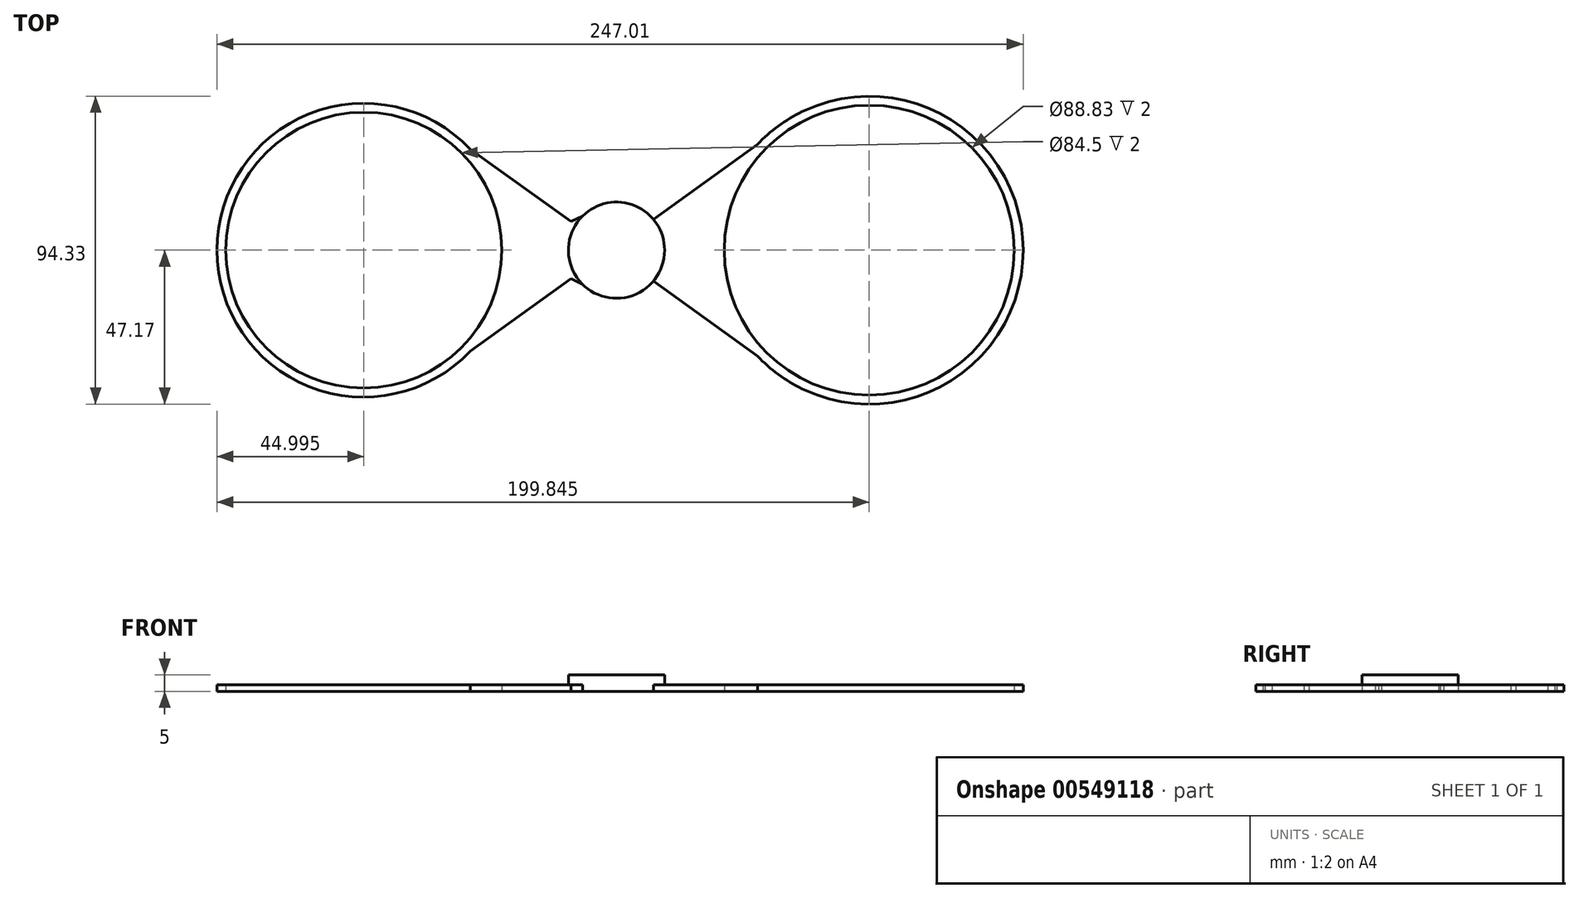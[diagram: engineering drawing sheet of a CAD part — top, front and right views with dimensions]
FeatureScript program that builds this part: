
annotation { "Feature Type Name" : "Feature", "Feature Type Description" : "" }
export const myFeature = defineFeature(function(context is Context, id is Id, definition is map)
    precondition{}
    {
        {
            var Q0;
            Q0=qCreatedBy(makeId("Top.planeOp"),FACE);
            var sketch = newSketch(context, id + "F0", { "sketchPlane" : qUnion([Q0])});
            skCircle(sketch, "E0", {"center": v(77.42, 0) * mm, "radius": 47.16 * mm});
            skCircle(sketch, "E1", {"center": v(-77.43, 0) * mm, "radius": 45 * mm});
            skCircle(sketch, "E2", {"center": v(-77.43, 0) * mm, "radius": 42.25 * mm});
            skCircle(sketch, "E3", {"center": v(77.42, 0) * mm, "radius": 44.41 * mm});
            skPoint(sketch, "E4", {"position": v(-32.43, 0) * mm});
            skPoint(sketch, "E5", {"position": v(30.26, 0) * mm});
            skLineSegment(sketch, "E6", {"start": v(-77.43, 0) * mm, "end": v(-58.4, 40.78) * mm});
            skLineSegment(sketch, "E7", {"start": v(-77.43, 0) * mm, "end": v(-58.4, -40.78) * mm});
            skLineSegment(sketch, "E8", {"start": v(77.42, 0) * mm, "end": v(57.5, -42.75) * mm});
            skLineSegment(sketch, "E9", {"start": v(77.42, 0) * mm, "end": v(57.5, 42.75) * mm});
            skLineSegment(sketch, "E10", {"start": v(-58.4, 40.78) * mm, "end": v(57.5, -42.75) * mm});
            skLineSegment(sketch, "E11", {"start": v(57.5, 42.75) * mm, "end": v(-58.4, -40.78) * mm});
            skLineSegment(sketch, "E12", {"start": v(-32.43, 0) * mm, "end": v(57.5, 42.75) * mm});
            skLineSegment(sketch, "E13", {"start": v(30.26, 0) * mm, "end": v(-58.4, -40.78) * mm});
            skLineSegment(sketch, "E14", {"start": v(-32.43, 0) * mm, "end": v(57.5, -42.75) * mm});
            skLineSegment(sketch, "E15", {"start": v(30.26, 0) * mm, "end": v(-58.4, 40.78) * mm});
            skSolve(sketch);
        }
        {
            var Q0;
            {var subQ1=sQuery(id+"F0.wireOp",EDGE,"E0");var subQ3=sQuery(id+"F0.wireOp",EDGE,"E10");var subQ4=makeQuery(id+"F0.imprint","INTERSECT",VERTEX,{"derivedFrom":[subQ1,subQ3]});Q0=makeQuery(id+"F0.imprint","IMPRINT",FACE,{"disambiguationData":[TD([[makeQuery(id+"F0.imprint","IMPRINT",EDGE,{"disambiguationData":[TD([[subQ4,1.0]])],"derivedFrom":subQ3}),1.0]])]});}
            var Q1;
            {var subQ1=sQuery(id+"F0.wireOp",EDGE,"E13");var subQ3=sQuery(id+"F0.wireOp",EDGE,"HmEMSvIh-oE6Y-JeN1-VhMK-6YFaZQDYRGXj");var subQ4=makeQuery(id+"F0.imprint","INTERSECT",VERTEX,{"disambiguationData":[OD(1.0)],"derivedFrom":[subQ1,subQ3]});Q1=makeQuery(id+"F0.imprint","IMPRINT",FACE,{"disambiguationData":[TD([[makeQuery(id+"F0.imprint","IMPRINT",EDGE,{"disambiguationData":[TD([[subQ4,-1.0]])],"derivedFrom":subQ3}),-1.0]])]});}
            var Q2;
            {var subQ1=sQuery(id+"F0.wireOp",EDGE,"E0");var subQ3=sQuery(id+"F0.wireOp",EDGE,"E11");var subQ4=makeQuery(id+"F0.imprint","INTERSECT",VERTEX,{"derivedFrom":[subQ1,subQ3]});Q2=makeQuery(id+"F0.imprint","IMPRINT",FACE,{"disambiguationData":[TD([[makeQuery(id+"F0.imprint","IMPRINT",EDGE,{"disambiguationData":[TD([[subQ4,-1.0]])],"derivedFrom":subQ3}),1.0]])]});}
            var Q3;
            {var subQ1=sQuery(id+"F0.wireOp",EDGE,"E1");var subQ3=sQuery(id+"F0.wireOp",EDGE,"E10");var subQ4=makeQuery(id+"F0.imprint","INTERSECT",VERTEX,{"derivedFrom":[subQ1,subQ3]});Q3=makeQuery(id+"F0.imprint","IMPRINT",FACE,{"disambiguationData":[TD([[makeQuery(id+"F0.imprint","IMPRINT",EDGE,{"disambiguationData":[TD([[subQ4,-1.0]])],"derivedFrom":subQ3}),-1.0]])]});}
            var Q4;
            {var subQ1=sQuery(id+"F0.wireOp",EDGE,"E12");var subQ3=sQuery(id+"F0.wireOp",EDGE,"HmEMSvIh-oE6Y-JeN1-VhMK-6YFaZQDYRGXj");var subQ4=makeQuery(id+"F0.imprint","INTERSECT",VERTEX,{"disambiguationData":[OD(1.0)],"derivedFrom":[subQ1,subQ3]});Q4=makeQuery(id+"F0.imprint","IMPRINT",FACE,{"disambiguationData":[TD([[makeQuery(id+"F0.imprint","IMPRINT",EDGE,{"disambiguationData":[TD([[subQ4,-1.0]])],"derivedFrom":subQ3}),-1.0]])]});}
            var Q5;
            {var subQ1=sQuery(id+"F0.wireOp",EDGE,"E1");var subQ3=sQuery(id+"F0.wireOp",EDGE,"E11");var subQ4=makeQuery(id+"F0.imprint","INTERSECT",VERTEX,{"derivedFrom":[subQ1,subQ3]});Q5=makeQuery(id+"F0.imprint","IMPRINT",FACE,{"disambiguationData":[TD([[makeQuery(id+"F0.imprint","IMPRINT",EDGE,{"disambiguationData":[TD([[subQ4,1.0]])],"derivedFrom":subQ3}),-1.0]])]});}
            var Q6;
            {var subQ5=sQuery(id+"F0.wireOp",EDGE,"E12");var subQ6=sQuery(id+"F0.wireOp",EDGE,"E10");var subQ7=makeQuery(id+"F0.imprint","INTERSECT",VERTEX,{"derivedFrom":[subQ6,subQ5]});Q6=makeQuery(id+"F0.imprint","IMPRINT",FACE,{"disambiguationData":[TD([[makeQuery(id+"F0.imprint","IMPRINT",EDGE,{"disambiguationData":[TD([[subQ7,-1.0]])],"derivedFrom":subQ6}),-1.0]])]});}
            var Q7;
            {var subQ1=sQuery(id+"F0.wireOp",EDGE,"E11");var subQ6=sQuery(id+"F0.wireOp",EDGE,"E10");var subQ9=makeQuery(id+"F0.imprint","INTERSECT",VERTEX,{"derivedFrom":[subQ6,subQ1]});Q7=makeQuery(id+"F0.imprint","IMPRINT",FACE,{"disambiguationData":[TD([[makeQuery(id+"F0.imprint","IMPRINT",EDGE,{"disambiguationData":[TD([[subQ9,-1.0]])],"derivedFrom":subQ6}),1.0]])]});}
            var Q8;
            {var subQ0=sQuery(id+"F0.wireOp",EDGE,"E12");var subQ1=sQuery(id+"F0.wireOp",EDGE,"E10");var subQ2=makeQuery(id+"F0.imprint","INTERSECT",VERTEX,{"derivedFrom":[subQ1,subQ0]});Q8=makeQuery(id+"F0.imprint","IMPRINT",FACE,{"disambiguationData":[TD([[makeQuery(id+"F0.imprint","IMPRINT",EDGE,{"disambiguationData":[TD([[subQ2,-1.0]])],"derivedFrom":subQ1}),1.0]])]});}
            var Q9;
            {var subQ0=sQuery(id+"F0.wireOp",EDGE,"E11");var subQ1=sQuery(id+"F0.wireOp",EDGE,"E10");var subQ2=makeQuery(id+"F0.imprint","INTERSECT",VERTEX,{"derivedFrom":[subQ1,subQ0]});Q9=makeQuery(id+"F0.imprint","IMPRINT",FACE,{"disambiguationData":[TD([[makeQuery(id+"F0.imprint","IMPRINT",EDGE,{"disambiguationData":[TD([[subQ2,-1.0]])],"derivedFrom":subQ1}),-1.0]])]});}
            extrude(context, id + "F1", {"entities" : qUnion([Q0, Q1, Q2, Q3, Q4, Q5, Q6, Q7, Q8, Q9]), "depth" : 2 * mm, "offsetDistance" : 25 * mm});
        }
        {
            var Q0;
            {var subQ1=sQuery(id+"F0.wireOp",EDGE,"E6");var subQ4=sQuery(id+"F0.wireOp",EDGE,"E2");var subQ5=makeQuery(id+"F0.imprint","INTERSECT",VERTEX,{"derivedFrom":[subQ4,subQ1]});Q0=makeQuery(id+"F0.imprint","IMPRINT",FACE,{"disambiguationData":[TD([[makeQuery(id+"F0.imprint","IMPRINT",EDGE,{"disambiguationData":[TD([[subQ5,1.0]])],"derivedFrom":subQ4}),-1.0]])]});}
            var Q1;
            {var subQ0=sQuery(id+"F0.wireOp",EDGE,"E13");var subQ1=sQuery(id+"F0.wireOp",EDGE,"E1");var subQ2=makeQuery(id+"F0.imprint","INTERSECT",VERTEX,{"derivedFrom":[subQ1,subQ0]});Q1=makeQuery(id+"F0.imprint","IMPRINT",FACE,{"disambiguationData":[TD([[makeQuery(id+"F0.imprint","IMPRINT",EDGE,{"disambiguationData":[TD([[subQ2,-1.0]])],"derivedFrom":subQ1}),1.0]])]});}
            var Q2;
            {var subQ0=sQuery(id+"F0.wireOp",EDGE,"E15");var subQ1=sQuery(id+"F0.wireOp",EDGE,"E1");var subQ2=makeQuery(id+"F0.imprint","INTERSECT",VERTEX,{"derivedFrom":[subQ1,subQ0]});Q2=makeQuery(id+"F0.imprint","IMPRINT",FACE,{"disambiguationData":[TD([[makeQuery(id+"F0.imprint","IMPRINT",EDGE,{"disambiguationData":[TD([[subQ2,1.0]])],"derivedFrom":subQ1}),1.0]])]});}
            var Q3;
            {var subQ0=sQuery(id+"F0.wireOp",EDGE,"E12");var subQ1=sQuery(id+"F0.wireOp",EDGE,"E0");var subQ2=makeQuery(id+"F0.imprint","INTERSECT",VERTEX,{"derivedFrom":[subQ1,subQ0]});Q3=makeQuery(id+"F0.imprint","IMPRINT",FACE,{"disambiguationData":[TD([[makeQuery(id+"F0.imprint","IMPRINT",EDGE,{"disambiguationData":[TD([[subQ2,-1.0]])],"derivedFrom":subQ1}),1.0]])]});}
            var Q4;
            {var subQ0=sQuery(id+"F0.wireOp",EDGE,"E8");var subQ1=sQuery(id+"F0.wireOp",EDGE,"E3");var subQ2=makeQuery(id+"F0.imprint","INTERSECT",VERTEX,{"derivedFrom":[subQ1,subQ0]});Q4=makeQuery(id+"F0.imprint","IMPRINT",FACE,{"disambiguationData":[TD([[makeQuery(id+"F0.imprint","IMPRINT",EDGE,{"disambiguationData":[TD([[subQ2,1.0]])],"derivedFrom":subQ1}),-1.0]])]});}
            var Q5;
            {var subQ0=sQuery(id+"F0.wireOp",EDGE,"E14");var subQ1=sQuery(id+"F0.wireOp",EDGE,"E0");var subQ2=makeQuery(id+"F0.imprint","INTERSECT",VERTEX,{"derivedFrom":[subQ1,subQ0]});Q5=makeQuery(id+"F0.imprint","IMPRINT",FACE,{"disambiguationData":[TD([[makeQuery(id+"F0.imprint","IMPRINT",EDGE,{"disambiguationData":[TD([[subQ2,1.0]])],"derivedFrom":subQ1}),1.0]])]});}
            var Q6;
            {var subQ0=sQuery(id+"F0.wireOp",EDGE,"E6");var subQ5=sQuery(id+"F0.wireOp",EDGE,"E2");var subQ6=makeQuery(id+"F0.imprint","INTERSECT",VERTEX,{"derivedFrom":[subQ5,subQ0]});Q6=makeQuery(id+"F0.imprint","IMPRINT",FACE,{"disambiguationData":[TD([[makeQuery(id+"F0.imprint","IMPRINT",EDGE,{"disambiguationData":[TD([[subQ6,-1.0]])],"derivedFrom":subQ5}),-1.0]])]});}
            var Q7;
            {var subQ0=sQuery(id+"F0.wireOp",EDGE,"E8");var subQ5=sQuery(id+"F0.wireOp",EDGE,"E3");var subQ6=makeQuery(id+"F0.imprint","INTERSECT",VERTEX,{"derivedFrom":[subQ5,subQ0]});Q7=makeQuery(id+"F0.imprint","IMPRINT",FACE,{"disambiguationData":[TD([[makeQuery(id+"F0.imprint","IMPRINT",EDGE,{"disambiguationData":[TD([[subQ6,-1.0]])],"derivedFrom":subQ5}),-1.0]])]});}
            extrude(context, id + "F2", {"entities" : qUnion([Q0, Q1, Q2, Q3, Q4, Q5, Q6, Q7]), "operationType" : NewBodyOperationType.ADD, "depth" : 2 * mm, "offsetDistance" : 25 * mm});
        }
        {
            var Q0;
            Q0=makeQuery(id+"F1.opExtrude","CAP_FACE",FACE,{"disambiguationData":[OSD([sQuery(id+"F0.wireOp",EDGE,"E0"),sQuery(id+"F0.wireOp",EDGE,"E1"),sQuery(id+"F0.wireOp",EDGE,"E10"),sQuery(id+"F0.wireOp",EDGE,"E11"),sQuery(id+"F0.wireOp",EDGE,"E12"),sQuery(id+"F0.wireOp",EDGE,"E13"),sQuery(id+"F0.wireOp",EDGE,"E14"),sQuery(id+"F0.wireOp",EDGE,"E15")])],"isStart":false});
            var sketch = newSketch(context, id + "F3", { "sketchPlane" : qUnion([Q0])});
            skCircle(sketch, "E16", {"center": v(0, 0) * mm, "radius": 14.74 * mm});
            skSolve(sketch);
        }
        {
            var Q0;
            {var subQ0=sQuery(id+"F3.wireOp",EDGE,"E16");var subQ2=makeQuery(id+"F1.opExtrude","CAP_EDGE",EDGE,{"disambiguationData":[OSD([sQuery(id+"F0.wireOp",EDGE,"E12")])],"isStart":false});var subQ4=makeQuery(id+"F3.imprint","INTERSECT",VERTEX,{"derivedFrom":[subQ2,subQ0]});Q0=makeQuery(id+"F3.imprint","IMPRINT",FACE,{"disambiguationData":[TD([[makeQuery(id+"F3.imprint","IMPRINT",EDGE,{"disambiguationData":[TD([[subQ4,-1.0]])],"derivedFrom":subQ0}),1.0]])]});}
            var Q1;
            {var subQ0=sQuery(id+"F3.wireOp",EDGE,"E16");var subQ1=makeQuery(id+"F1.opExtrude","CAP_EDGE",EDGE,{"disambiguationData":[OSD([sQuery(id+"F0.wireOp",EDGE,"E15")])],"isStart":false});var subQ3=makeQuery(id+"F3.imprint","INTERSECT",VERTEX,{"derivedFrom":[subQ1,subQ0]});Q1=makeQuery(id+"F3.imprint","IMPRINT",FACE,{"disambiguationData":[TD([[makeQuery(id+"F3.imprint","IMPRINT",EDGE,{"disambiguationData":[TD([[subQ3,-1.0]])],"derivedFrom":subQ0}),1.0]])]});}
            var Q2;
            {var subQ0=sQuery(id+"F3.wireOp",EDGE,"E16");var subQ1=makeQuery(id+"F1.opExtrude","CAP_EDGE",EDGE,{"disambiguationData":[OSD([sQuery(id+"F0.wireOp",EDGE,"E12")])],"isStart":false});var subQ3=makeQuery(id+"F3.imprint","INTERSECT",VERTEX,{"derivedFrom":[subQ1,subQ0]});Q2=makeQuery(id+"F3.imprint","IMPRINT",FACE,{"disambiguationData":[TD([[makeQuery(id+"F3.imprint","IMPRINT",EDGE,{"disambiguationData":[TD([[subQ3,1.0]])],"derivedFrom":subQ0}),1.0]])]});}
            var Q3;
            {var subQ0=sQuery(id+"F3.wireOp",EDGE,"E16");var subQ1=makeQuery(id+"F1.opExtrude","CAP_EDGE",EDGE,{"disambiguationData":[OSD([sQuery(id+"F0.wireOp",EDGE,"E14")])],"isStart":false});var subQ3=makeQuery(id+"F3.imprint","INTERSECT",VERTEX,{"derivedFrom":[subQ1,subQ0]});Q3=makeQuery(id+"F3.imprint","IMPRINT",FACE,{"disambiguationData":[TD([[makeQuery(id+"F3.imprint","IMPRINT",EDGE,{"disambiguationData":[TD([[subQ3,-1.0]])],"derivedFrom":subQ0}),1.0]])]});}
            var Q4;
            {var subQ0=sQuery(id+"F3.wireOp",EDGE,"E16");var subQ1=makeQuery(id+"F1.opExtrude","CAP_EDGE",EDGE,{"disambiguationData":[OSD([sQuery(id+"F0.wireOp",EDGE,"E13")])],"isStart":false});var subQ3=makeQuery(id+"F3.imprint","INTERSECT",VERTEX,{"derivedFrom":[subQ1,subQ0]});Q4=makeQuery(id+"F3.imprint","IMPRINT",FACE,{"disambiguationData":[TD([[makeQuery(id+"F3.imprint","IMPRINT",EDGE,{"disambiguationData":[TD([[subQ3,1.0]])],"derivedFrom":subQ0}),1.0]])]});}
            var Q5;
            {var subQ1=sQuery(id+"F0.wireOp",EDGE,"E13");var subQ2=makeQuery(id+"F1.opExtrude","CAP_EDGE",EDGE,{"disambiguationData":[OSD([subQ1])],"isStart":false});Q5=makeQuery(id+"F3.imprint","IMPRINT",FACE,{"disambiguationData":[TD([[makeQuery(id+"F3.imprint","IMPRINT",EDGE,{"derivedFrom":subQ2}),1.0]])]});}
            var Q6;
            {var subQ1=sQuery(id+"F0.wireOp",EDGE,"E15");var subQ2=makeQuery(id+"F1.opExtrude","CAP_EDGE",EDGE,{"disambiguationData":[OSD([subQ1])],"isStart":false});Q6=makeQuery(id+"F3.imprint","IMPRINT",FACE,{"disambiguationData":[TD([[makeQuery(id+"F3.imprint","IMPRINT",EDGE,{"derivedFrom":subQ2}),-1.0]])]});}
            extrude(context, id + "F4", {"entities" : qUnion([Q0, Q1, Q2, Q3, Q4, Q5, Q6]), "operationType" : NewBodyOperationType.ADD, "depth" : 3 * mm, "offsetDistance" : 25 * mm});
        }
        {
            var Q0;
            {var subQ0=sQuery(id+"F3.wireOp",EDGE,"E16");var subQ1=sQuery(id+"F0.wireOp",EDGE,"E13");var subQ2=sQuery(id+"F0.wireOp",EDGE,"E14");var subQ3=makeQuery(id+"F4.opExtrude","CAP_FACE",FACE,{"disambiguationData":[OSD([subQ0])],"isStart":true});Q0=makeQuery(id+"F4.boolean.opBoolean","SPLIT",FACE,{"disambiguationData":[TD([makeQuery(id+"F1.opExtrude","CAP_FACE",FACE,{"disambiguationData":[OSD([sQuery(id+"F0.wireOp",EDGE,"E0"),sQuery(id+"F0.wireOp",EDGE,"E1"),sQuery(id+"F0.wireOp",EDGE,"E10"),sQuery(id+"F0.wireOp",EDGE,"E11"),sQuery(id+"F0.wireOp",EDGE,"E12"),subQ1,subQ2,sQuery(id+"F0.wireOp",EDGE,"E15")])],"isStart":false}),makeQuery(id+"F1.opExtrude","SWEPT_FACE",FACE,{"disambiguationData":[OSD([subQ1])]}),makeQuery(id+"F1.opExtrude","SWEPT_FACE",FACE,{"disambiguationData":[OSD([subQ2])]}),makeQuery(id+"F4.opExtrude","SWEPT_FACE",FACE,{"disambiguationData":[OSD([subQ0])]}),subQ3]),OD(0.0)],"derivedFrom":subQ3});}
            var Q1;
            {var subQ0=sQuery(id+"F3.wireOp",EDGE,"E16");var subQ1=sQuery(id+"F0.wireOp",EDGE,"E15");var subQ2=sQuery(id+"F0.wireOp",EDGE,"E12");var subQ3=makeQuery(id+"F4.opExtrude","CAP_FACE",FACE,{"disambiguationData":[OSD([subQ0])],"isStart":true});Q1=makeQuery(id+"F4.boolean.opBoolean","SPLIT",FACE,{"disambiguationData":[TD([makeQuery(id+"F1.opExtrude","CAP_FACE",FACE,{"disambiguationData":[OSD([sQuery(id+"F0.wireOp",EDGE,"E0"),sQuery(id+"F0.wireOp",EDGE,"E1"),sQuery(id+"F0.wireOp",EDGE,"E10"),sQuery(id+"F0.wireOp",EDGE,"E11"),subQ2,sQuery(id+"F0.wireOp",EDGE,"E13"),sQuery(id+"F0.wireOp",EDGE,"E14"),subQ1])],"isStart":false}),makeQuery(id+"F1.opExtrude","SWEPT_FACE",FACE,{"disambiguationData":[OSD([subQ2])]}),makeQuery(id+"F1.opExtrude","SWEPT_FACE",FACE,{"disambiguationData":[OSD([subQ1])]}),makeQuery(id+"F4.opExtrude","SWEPT_FACE",FACE,{"disambiguationData":[OSD([subQ0])]}),subQ3]),OD(1.0)],"derivedFrom":subQ3});}
            var Q2;
            {var subQ0=sQuery(id+"F3.wireOp",EDGE,"E16");var subQ1=sQuery(id+"F0.wireOp",EDGE,"E15");var subQ2=sQuery(id+"F0.wireOp",EDGE,"E12");var subQ3=makeQuery(id+"F4.opExtrude","CAP_FACE",FACE,{"disambiguationData":[OSD([subQ0])],"isStart":true});Q2=makeQuery(id+"F4.boolean.opBoolean","SPLIT",FACE,{"disambiguationData":[TD([makeQuery(id+"F1.opExtrude","CAP_FACE",FACE,{"disambiguationData":[OSD([sQuery(id+"F0.wireOp",EDGE,"E0"),sQuery(id+"F0.wireOp",EDGE,"E1"),sQuery(id+"F0.wireOp",EDGE,"E10"),sQuery(id+"F0.wireOp",EDGE,"E11"),subQ2,sQuery(id+"F0.wireOp",EDGE,"E13"),sQuery(id+"F0.wireOp",EDGE,"E14"),subQ1])],"isStart":false}),makeQuery(id+"F1.opExtrude","SWEPT_FACE",FACE,{"disambiguationData":[OSD([subQ2])]}),makeQuery(id+"F1.opExtrude","SWEPT_FACE",FACE,{"disambiguationData":[OSD([subQ1])]}),makeQuery(id+"F4.opExtrude","SWEPT_FACE",FACE,{"disambiguationData":[OSD([subQ0])]}),subQ3]),OD(0.0)],"derivedFrom":subQ3});}
            var Q3;
            {var subQ0=sQuery(id+"F3.wireOp",EDGE,"E16");var subQ1=sQuery(id+"F0.wireOp",EDGE,"E13");var subQ2=sQuery(id+"F0.wireOp",EDGE,"E14");var subQ3=makeQuery(id+"F4.opExtrude","CAP_FACE",FACE,{"disambiguationData":[OSD([subQ0])],"isStart":true});Q3=makeQuery(id+"F4.boolean.opBoolean","SPLIT",FACE,{"disambiguationData":[TD([makeQuery(id+"F1.opExtrude","CAP_FACE",FACE,{"disambiguationData":[OSD([sQuery(id+"F0.wireOp",EDGE,"E0"),sQuery(id+"F0.wireOp",EDGE,"E1"),sQuery(id+"F0.wireOp",EDGE,"E10"),sQuery(id+"F0.wireOp",EDGE,"E11"),sQuery(id+"F0.wireOp",EDGE,"E12"),subQ1,subQ2,sQuery(id+"F0.wireOp",EDGE,"E15")])],"isStart":false}),makeQuery(id+"F1.opExtrude","SWEPT_FACE",FACE,{"disambiguationData":[OSD([subQ1])]}),makeQuery(id+"F1.opExtrude","SWEPT_FACE",FACE,{"disambiguationData":[OSD([subQ2])]}),makeQuery(id+"F4.opExtrude","SWEPT_FACE",FACE,{"disambiguationData":[OSD([subQ0])]}),subQ3]),OD(1.0)],"derivedFrom":subQ3});}
            var Q4;
            {var subQ0=sQuery(id+"F0.wireOp",EDGE,"E12");var subQ1=sQuery(id+"F0.wireOp",EDGE,"E15");var subQ2=sQuery(id+"F0.wireOp",EDGE,"E11");var subQ3=sQuery(id+"F0.wireOp",EDGE,"E0");var subQ4=sQuery(id+"F0.wireOp",EDGE,"E14");var subQ5=sQuery(id+"F0.wireOp",EDGE,"E1");var subQ6=sQuery(id+"F3.wireOp",EDGE,"E16");var subQ7=makeQuery(id+"F4.opExtrude","CAP_FACE",FACE,{"disambiguationData":[OSD([subQ6])],"isStart":true});Q4=makeQuery(id+"F4.boolean.opBoolean","SPLIT",FACE,{"disambiguationData":[TD([makeQuery(id+"F1.opExtrude","CAP_FACE",FACE,{"disambiguationData":[OSD([subQ3,subQ5,sQuery(id+"F0.wireOp",EDGE,"E10"),subQ2,subQ0,sQuery(id+"F0.wireOp",EDGE,"E13"),subQ4,subQ1])],"isStart":false}),makeQuery(id+"F1.opExtrude","SWEPT_FACE",FACE,{"disambiguationData":[OSD([subQ2]),TDD([makeQuery(id+"F0.imprint","IMPRINT",EDGE,{"disambiguationData":[TD([[makeQuery(id+"F0.imprint","INTERSECT",VERTEX,{"derivedFrom":[subQ3,subQ2]}),-1.0]])],"derivedFrom":subQ2})])]}),makeQuery(id+"F1.opExtrude","SWEPT_FACE",FACE,{"disambiguationData":[OSD([subQ0])]}),makeQuery(id+"F1.opExtrude","SWEPT_FACE",FACE,{"disambiguationData":[OSD([subQ1])]}),makeQuery(id+"F2.opExtrude","CAP_FACE",FACE,{"disambiguationData":[OSD([subQ3,sQuery(id+"F0.wireOp",EDGE,"E3"),subQ0,subQ4])],"isStart":false}),makeQuery(id+"F2.opExtrude","CAP_FACE",FACE,{"disambiguationData":[OSD([subQ5,sQuery(id+"F0.wireOp",EDGE,"E2")])],"isStart":false}),makeQuery(id+"F4.opExtrude","SWEPT_FACE",FACE,{"disambiguationData":[OSD([subQ6])]}),subQ7])],"derivedFrom":subQ7});}
            var Q5;
            {var subQ0=sQuery(id+"F0.wireOp",EDGE,"E13");var subQ1=sQuery(id+"F3.wireOp",EDGE,"E16");var subQ2=sQuery(id+"F0.wireOp",EDGE,"E14");var subQ3=sQuery(id+"F0.wireOp",EDGE,"E1");var subQ4=makeQuery(id+"F4.opExtrude","CAP_FACE",FACE,{"disambiguationData":[OSD([subQ1])],"isStart":true});var subQ5=sQuery(id+"F0.wireOp",EDGE,"E10");var subQ6=sQuery(id+"F0.wireOp",EDGE,"E0");var subQ7=sQuery(id+"F0.wireOp",EDGE,"E12");Q5=makeQuery(id+"F4.boolean.opBoolean","SPLIT",FACE,{"disambiguationData":[TD([makeQuery(id+"F1.opExtrude","CAP_FACE",FACE,{"disambiguationData":[OSD([subQ6,subQ3,subQ5,sQuery(id+"F0.wireOp",EDGE,"E11"),subQ7,subQ0,subQ2,sQuery(id+"F0.wireOp",EDGE,"E15")])],"isStart":false}),makeQuery(id+"F1.opExtrude","SWEPT_FACE",FACE,{"disambiguationData":[OSD([subQ5]),TDD([makeQuery(id+"F0.imprint","IMPRINT",EDGE,{"disambiguationData":[TD([[makeQuery(id+"F0.imprint","INTERSECT",VERTEX,{"derivedFrom":[subQ6,subQ5]}),1.0]])],"derivedFrom":subQ5})])]}),makeQuery(id+"F1.opExtrude","SWEPT_FACE",FACE,{"disambiguationData":[OSD([subQ0])]}),makeQuery(id+"F1.opExtrude","SWEPT_FACE",FACE,{"disambiguationData":[OSD([subQ2])]}),makeQuery(id+"F2.opExtrude","CAP_FACE",FACE,{"disambiguationData":[OSD([subQ6,sQuery(id+"F0.wireOp",EDGE,"E3"),subQ7,subQ2])],"isStart":false}),makeQuery(id+"F2.opExtrude","CAP_FACE",FACE,{"disambiguationData":[OSD([subQ3,sQuery(id+"F0.wireOp",EDGE,"E2")])],"isStart":false}),makeQuery(id+"F4.opExtrude","SWEPT_FACE",FACE,{"disambiguationData":[OSD([subQ1])]}),subQ4])],"derivedFrom":subQ4});}
            extrude(context, id + "F5", {"entities" : qUnion([Q0, Q1, Q2, Q3, Q4, Q5]), "operationType" : NewBodyOperationType.ADD, "depth" : 2 * mm, "offsetDistance" : 25 * mm});
        }
    });
